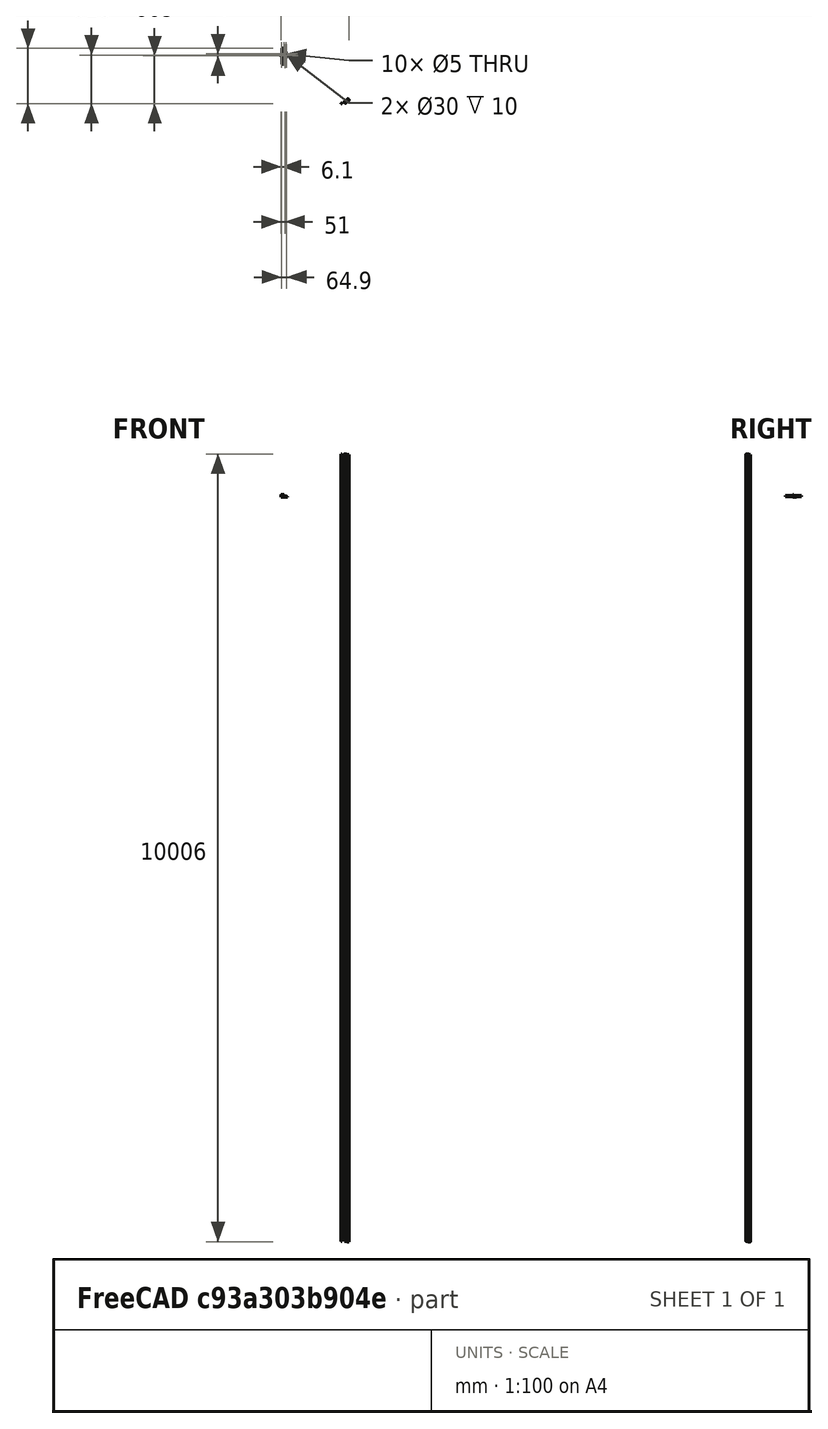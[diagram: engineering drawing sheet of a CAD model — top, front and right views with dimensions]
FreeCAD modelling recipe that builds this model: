
FCSTD DOCUMENT  (FreeCAD 0.14R3702 (Git))
Label: slide_rail_flange_mount
License: CC-BY 3.0
LicenseURL: http://creativecommons.org/licenses/by/3.0/
objects: Sketcher::SketchObject×6, PartDesign::Pocket×5, Mesh::Feature×2, Part::Cylinder×2, Part::Box×2, PartDesign::Fillet×2, PartDesign::Chamfer×2, PartDesign::Pad×1, Part::MultiFuse×1, Part::Feature×1
note: 28 computed .brp shape members not serialized (recipe doc carries the construction recipe); baked Part::Feature solids carry a one-line shape summary decoded from their .brp

FEATURE [Mesh::Feature] tmp  label="plate"
FEATURE [Part::Cylinder] Cylinder  label="bearing"
  Angle = 360
  Height = 9
  Placement = pos=(-717,613,-534) rot=(0,0,1;0rad)
  Radius = 15
FEATURE [Mesh::Feature] lead_screw_flange  label="lead-screw-flange"
  Placement = pos=(-747,556,-523) rot=(0,0.707107,0.707107;3.14159rad)
FEATURE [Part::Cylinder] Cylinder001  label="lead_screw"
  Angle = 360
  Height = 200
  Placement = pos=(-747,700,-523) rot=(1,0,0;1.5708rad)
  Radius = 5.556
FEATURE [Sketcher::SketchObject] Sketch
  Placement = pos=(-717,613,-525) rot=(0,0,1;0rad)
  Support = -> Cylinder [Face2]
  sketch-geometry (1):
    g0: Circle CenterX=0 CenterY=0 CenterZ=0 NormalX=0 NormalY=0 NormalZ=1 Radius=5
  constraints (2):
    c: Radius(g0) = 5
    c: Coincident(g0,g-1)
FEATURE [PartDesign::Pocket] Pocket
  Length = 5
  Placement = pos=(-717,613,-534) rot=(0,0,1;0rad)
  Sketch = -> Sketch
  Type = 1
FEATURE [Part::Box] Box  label="Cube"
  Height = 4
  Length = 80
  Placement = pos=(-768,594,-534) rot=(0,0,1;0rad)
  Width = 42
FEATURE [Sketcher::SketchObject] Sketch001
  Placement = pos=(-768,594,-530) rot=(0,0,1;0rad)
  Support = -> Box [Face6]
  sketch-geometry (1):
    g0: Circle CenterX=82 CenterY=41 CenterZ=0 NormalX=0 NormalY=0 NormalZ=1 Radius=15
  constraints (3):
    c: DistanceX(g-1,g0) = 82
    c: DistanceY(g-1,g0) = 41
    c: Radius(g0) = 15
FEATURE [PartDesign::Pocket] Pocket001
  Length = 5
  Placement = pos=(-768,594,-534) rot=(0,0,1;0rad)
  Sketch = -> Sketch001
  Type = 1
FEATURE [Part::Box] Box001  label="Cube001"
  Height = 25
  Length = 40
  Placement = pos=(-768,594,-530) rot=(0,0,1;0rad)
  Width = 4
FEATURE [Sketcher::SketchObject] Sketch002
  Placement = pos=(-768,598,-530) rot=(0,0.707107,0.707107;3.14159rad)
  Support = -> Box001 [Face4]
  sketch-geometry (6):
    g0: Circle CenterX=-33.247 CenterY=14 CenterZ=0 NormalX=0 NormalY=0 NormalZ=1 Radius=2.5781
    g1: Circle CenterX=-8.5 CenterY=14 CenterZ=0 NormalX=0 NormalY=0 NormalZ=1 Radius=2.5781
    g2: ArcOfCircle CenterX=-20.85 CenterY=12 CenterZ=0 NormalX=0 NormalY=0 NormalZ=1 Radius=7.15 StartAngle=0 EndAngle=3.14159
    g3: LineSegment StartX=-13.7 StartY=12 StartZ=0 EndX=-13.7 EndY=0 EndZ=0
    g4: LineSegment StartX=-28 StartY=12 StartZ=0 EndX=-28 EndY=0 EndZ=0
    g5: LineSegment StartX=-28 StartY=0 StartZ=0 EndX=-13.7 EndY=0 EndZ=0
  constraints (21):
    c: Radius(g0) = 2.5781
    c: Equal(g0,g1)
    c: DistanceY(g-1,g0) = 14
    c: DistanceY(g-1,g1) = 14
    c: DistanceX(g0,g1) = 24.747
    c: DistanceX(g-1,g1) = -8.5
    c: DistanceY(g-1,g2) = 12
    c: DistanceX(g-1,g2) = -20.85
    c: DistanceY(g-1,g2) = 12
    c: DistanceY(g-1,g2) = 12
    c: DistanceX(g-1,g2) = -28
    c: PointOnObject(g3,g-1)
    c: Vertical(g3)
    c: Tangent(g3,g2)
    c: PointOnObject(g4,g-1)
    c: Vertical(g4)
    c: Tangent(g4,g2)
    c: Coincident(g2,g4)
    c: Coincident(g3,g2)
    c: Coincident(g5,g4)
    c: Coincident(g5,g3)
FEATURE [PartDesign::Pocket] Pocket002
  Length = 5
  Placement = pos=(-768,594,-530) rot=(0,0,1;0rad)
  Sketch = -> Sketch002
  Type = 1
FEATURE [PartDesign::Fillet] Fillet
  Base = -> Pocket002 [Edge15]
  Placement = pos=(-768,594,-530) rot=(0,0,1;0rad)
  Radius = 10
FEATURE [PartDesign::Fillet] Fillet001
  Base = -> Fillet [Edge20]
  Placement = pos=(-768,594,-530) rot=(0,0,1;0rad)
  Radius = 10
FEATURE [Sketcher::SketchObject] Sketch003
  Placement = pos=(-768,594,-530) rot=(0,0,1;0rad)
  Support = -> Pocket001 [Face3]
  sketch-geometry (1):
    g0: Circle CenterX=51 CenterY=19 CenterZ=0 NormalX=0 NormalY=0 NormalZ=1 Radius=17
  constraints (3):
    c: Radius(g0) = 17
    c: DistanceY(g-1,g0) = 19
    c: DistanceX(g-1,g0) = 51
FEATURE [PartDesign::Pad] Pad
  Length = 6
  Length2 = 100
  Placement = pos=(-768,594,-534) rot=(0,0,1;0rad)
  Sketch = -> Sketch003
  Type = 0
FEATURE [Sketcher::SketchObject] Sketch004
  Placement = pos=(-768,594,-524) rot=(0,0,1;0rad)
  Support = -> Pad [Face9]
  sketch-geometry (1):
    g0: Circle CenterX=51 CenterY=19 CenterZ=0 NormalX=0 NormalY=0 NormalZ=1 Radius=15
  constraints (3):
    c: Radius(g0) = 15
    c: DistanceX(g-1,g0) = 51
    c: DistanceY(g-1,g0) = 19
FEATURE [PartDesign::Pocket] Pocket003
  Length = 5
  Placement = pos=(-768,594,-534) rot=(0,0,1;0rad)
  Sketch = -> Sketch004
  Type = 1
FEATURE [Sketcher::SketchObject] Sketch005
  Placement = pos=(-768,594,-530) rot=(0,0,1;0rad)
  Support = -> Pocket003 [Face3]
  sketch-geometry (5):
    g0: Circle CenterX=6.1 CenterY=34 CenterZ=0 NormalX=0 NormalY=0 NormalZ=1 Radius=2.5
    g1: Circle CenterX=6.1 CenterY=14 CenterZ=0 NormalX=0 NormalY=0 NormalZ=1 Radius=2.5
    g2: Circle CenterX=35.9 CenterY=34 CenterZ=0 NormalX=0 NormalY=0 NormalZ=1 Radius=2.5
    g3: Circle CenterX=64 CenterY=36 CenterZ=0 NormalX=0 NormalY=0 NormalZ=1 Radius=2.5
    g4: Circle CenterX=71 CenterY=10 CenterZ=0 NormalX=0 NormalY=0 NormalZ=1 Radius=2.5
  constraints (15):
    c: Radius(g0) = 2.5
    c: Equal(g0,g1)
    c: Equal(g1,g2)
    c: Equal(g2,g3)
    c: Equal(g3,g4)
    c: DistanceY(g-1,g1) = 14
    c: DistanceY(g1,g0) = 20
    c: DistanceY(g-1,g4) = 10
    c: DistanceY(g3,g4) = -26
    c: DistanceY(g-1,g2) = 34
    c: DistanceX(g-1,g0) = 6.1
    c: DistanceX(g-1,g1) = 6.1
    c: DistanceX(g-1,g2) = 35.9
    c: DistanceX(g-1,g4) = 71
    c: DistanceX(g-1,g3) = 64
FEATURE [PartDesign::Pocket] Pocket004
  Length = 5
  Placement = pos=(-768,594,-534) rot=(0,0,1;0rad)
  Sketch = -> Sketch005
  Type = 1
FEATURE [Part::MultiFuse] Fusion
  Shapes = -> [Fillet001,Pocket004]
FEATURE [PartDesign::Chamfer] Chamfer
  Base = -> Fusion [Edge42]
  Size = 5
FEATURE [PartDesign::Chamfer] Chamfer001
  Base = -> Chamfer [Edge17]
  Size = 2
FEATURE [Part::Feature] Chamfer001001  label="Chamfer002"
  shape: bbox 80 x 42 x 29 mm, 27 faces (baked)
